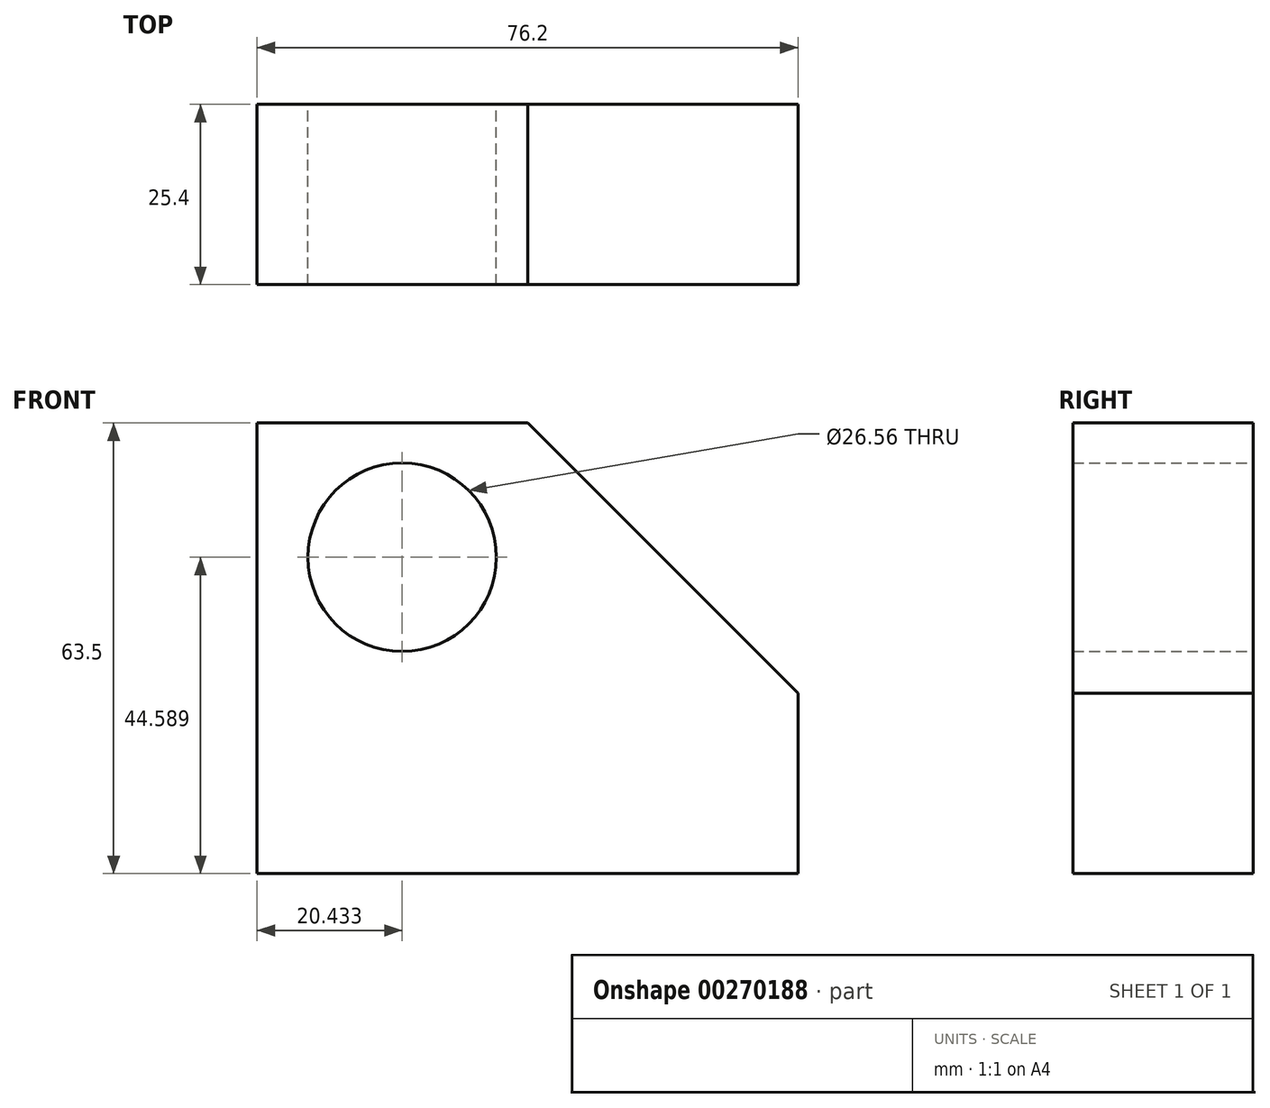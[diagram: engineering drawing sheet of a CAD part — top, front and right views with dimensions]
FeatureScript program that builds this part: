
annotation { "Feature Type Name" : "Feature", "Feature Type Description" : "" }
export const myFeature = defineFeature(function(context is Context, id is Id, definition is map)
    precondition{}
    {
        {
            var Q0;
            Q0=qCreatedBy(makeId("Front.planeOp"),FACE);
            var sketch = newSketch(context, id + "F0", { "sketchPlane" : qUnion([Q0])});
            skLineSegment(sketch, "E0", {"start": v(-25.4, 38.1) * mm, "end": v(-25.4, -25.4) * mm});
            skLineSegment(sketch, "E1", {"start": v(-25.4, 38.1) * mm, "end": v(12.7, 38.1) * mm});
            skLineSegment(sketch, "E2", {"start": v(12.7, 38.1) * mm, "end": v(50.8, 0) * mm});
            skLineSegment(sketch, "E3", {"start": v(-25.4, -25.4) * mm, "end": v(50.8, -25.4) * mm});
            skLineSegment(sketch, "E4", {"start": v(50.8, -25.4) * mm, "end": v(50.8, 0) * mm});
            skCircle(sketch, "E5", {"center": v(-4.97, 19.19) * mm, "radius": 13.28 * mm});
            skSolve(sketch);
        }
        {
            var Q0;
            Q0=qSketchRegion(id+"F0",true);
            extrude(context, id + "F1", {"entities" : qUnion([Q0]), "depth" : 25.4 * mm, "symmetric" : true});
        }
    });
